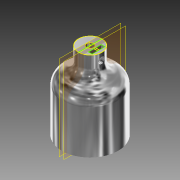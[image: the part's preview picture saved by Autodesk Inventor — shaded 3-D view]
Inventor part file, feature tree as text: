
AUTODESK INVENTOR PART (.ipt)
format: ipt  version: 2013 (Build 170138000, 138)  size: 180,224 bytes
history: native  units: mm
features: sketch x9, extrude x6, plane x4, fillet x2, other x1
ambient origin geometry x8: Origin, YZ Plane, XZ Plane, XY Plane, X Axis, Y Axis, Z Axis, Center Point
bodies: Solid1 (feature_tree)
feature tree (22):
  extrude  "Extrusion1"  Depth=3.0mm
  extrude  "Extrusion2"  Depth=10.0mm
  other  "Work Axis2"
  extrude  "Extrusion11"  Depth=20.0mm TaperAngle=0.0deg
  plane  "Work Plane6"
  sketch  "Sketch15"  dims[d87=90.0deg d88=3.0mm]
  plane  "Work Plane7"
  fillet  "Fillet3"  Radius=5.0mm
  fillet  "Fillet4"  Radius=5.0mm
  sketch  "Sketch17"  dims[d89=10.0mm d90=0.0mm d91=5.5mm]
  plane  "Work Plane8"
  extrude  "Extrusion13"  Depth=3.0mm
  sketch  "Sketch19"  dims[d95=2.0mm]
  plane  "Work Plane9"
  extrude  "Extrusion14"  Depth=5.5mm
  sketch  "Sketch21"  dims[d97=5.5mm d98=1.6mm d99=0.0mm d100=3.0mm d101=0.0mm]
  extrude  "Extrusion15"  Depth=1.6mm
  sketch  "Sketch1"  dims[d0=24.0mm d2=3.0mm]
  sketch  "Sketch2"  dims[d3=3.0mm d4=0.0mm d5=10.0mm]
  sketch  "Sketch14"  dims[d7=10.0mm d8=0.0mm d74=20.0mm d75=0.0mm d77=90.0deg d85=5.0mm d86=5.0mm]
  sketch  "Sketch18"  dims[d93=2.75mm d94=1.6mm]
  sketch  "Sketch20"  dims[d96=0.0mm]
